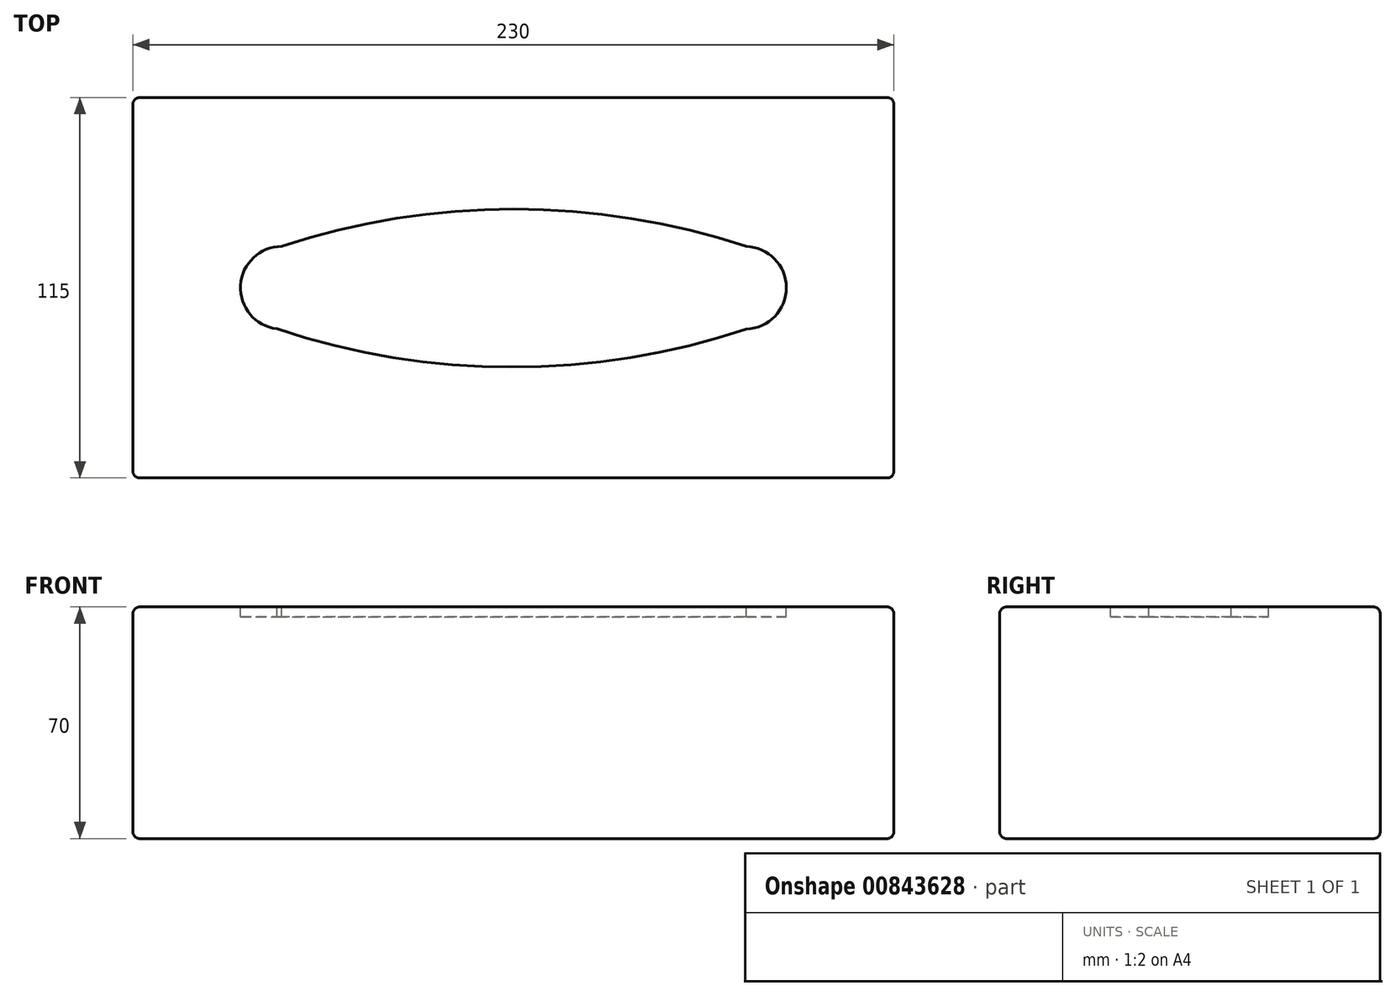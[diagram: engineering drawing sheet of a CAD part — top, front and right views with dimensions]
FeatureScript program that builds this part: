
annotation { "Feature Type Name" : "Feature", "Feature Type Description" : "" }
export const myFeature = defineFeature(function(context is Context, id is Id, definition is map)
    precondition{}
    {
        {
            var Q0;
            Q0=qCreatedBy(makeId("Top.planeOp"),FACE);
            var sketch = newSketch(context, id + "F0", { "sketchPlane" : qUnion([Q0])});
            skLineSegment(sketch, "E0.bottom", {"start": v(0, 0) * mm, "end": v(230, 0) * mm});
            skLineSegment(sketch, "E0.top", {"start": v(0, 115) * mm, "end": v(230, 115) * mm});
            skLineSegment(sketch, "E0.left", {"start": v(0, 0) * mm, "end": v(0, 115) * mm});
            skLineSegment(sketch, "E0.right", {"start": v(230, 0) * mm, "end": v(230, 115) * mm});
            skSolve(sketch);
        }
        {
            var Q0;
            Q0=makeQuery(id+"F0.imprint","IMPRINT",FACE,{"disambiguationData":[TD([[makeQuery(id+"F0.imprint","IMPRINT",EDGE,{"derivedFrom":sQuery(id+"F0.wireOp",EDGE,"E0.bottom")}),1.0]])]});
            extrude(context, id + "F1", {"entities" : qUnion([Q0]), "depth" : 70 * mm, "offsetDistance" : 25 * mm});
        }
        {
            var Q0;
            Q0=makeQuery(id+"F1.opExtrude","CAP_FACE",FACE,{"disambiguationData":[OSD([sQuery(id+"F0.wireOp",EDGE,"E0.bottom"),sQuery(id+"F0.wireOp",EDGE,"E0.top"),sQuery(id+"F0.wireOp",EDGE,"E0.left"),sQuery(id+"F0.wireOp",EDGE,"E0.right")])],"isStart":false});
            var Q1;
            Q1=makeQuery(id+"F1.opExtrude","CAP_FACE",FACE,{"disambiguationData":[OSD([sQuery(id+"F0.wireOp",EDGE,"E0.bottom"),sQuery(id+"F0.wireOp",EDGE,"E0.top"),sQuery(id+"F0.wireOp",EDGE,"E0.left"),sQuery(id+"F0.wireOp",EDGE,"E0.right")])],"isStart":true});
            var Q2;
            Q2=makeQuery(id+"F1.opExtrude","SWEPT_FACE",FACE,{"disambiguationData":[OSD([sQuery(id+"F0.wireOp",EDGE,"E0.right")])]});
            var Q3;
            Q3=makeQuery(id+"F1.opExtrude","SWEPT_FACE",FACE,{"disambiguationData":[OSD([sQuery(id+"F0.wireOp",EDGE,"E0.left")])]});
            fillet(context, id + "F2", {"entities" : qUnion([Q0, Q1, Q2, Q3]), "radius" : 2 * mm, "tangentPropagation" : true, "allowEdgeOverflow" : false});
        }
        {
            var Q0;
            Q0=makeQuery(id+"F1.opExtrude","CAP_FACE",FACE,{"disambiguationData":[OSD([sQuery(id+"F0.wireOp",EDGE,"E0.bottom"),sQuery(id+"F0.wireOp",EDGE,"E0.top"),sQuery(id+"F0.wireOp",EDGE,"E0.left"),sQuery(id+"F0.wireOp",EDGE,"E0.right")])],"isStart":false});
            var sketch = newSketch(context, id + "F3", { "sketchPlane" : qUnion([Q0])});
            skLineSegment(sketch, "E1", {"start": v(2, 57.5) * mm, "end": v(228, 57.5) * mm, "construction": true});
            skArc(sketch, "E2", {"start": v(44.98, 70) * mm, "mid": v(32.52, 58.22) * mm, "end": v(43.55, 45.08) * mm});
            skArc(sketch, "E3", {"start": v(185.43, 45) * mm, "mid": v(197.5, 57.54) * mm, "end": v(185.34, 70) * mm});
            skLineSegment(sketch, "E4", {"start": v(115, 57.5) * mm, "end": v(115, 92.59) * mm, "construction": true});
            skArc(sketch, "E5", {"start": v(185.34, 70) * mm, "mid": v(115.16, 81.29) * mm, "end": v(44.98, 70) * mm});
            skArc(sketch, "E6", {"start": v(43.55, 45.08) * mm, "mid": v(114.48, 33.51) * mm, "end": v(185.43, 45) * mm});
            skSolve(sketch);
        }
        {
            var Q0;
            Q0=makeQuery(id+"F3.imprint","IMPRINT",FACE,{"disambiguationData":[TD([[makeQuery(id+"F3.imprint","IMPRINT",EDGE,{"derivedFrom":sQuery(id+"F3.wireOp",EDGE,"E2")}),1.0]])]});
            extrude(context, id + "F4", {"entities" : qUnion([Q0]), "operationType" : NewBodyOperationType.REMOVE, "oppositeDirection" : true, "depth" : 3 * mm, "offsetDistance" : 25 * mm});
        }
    });
